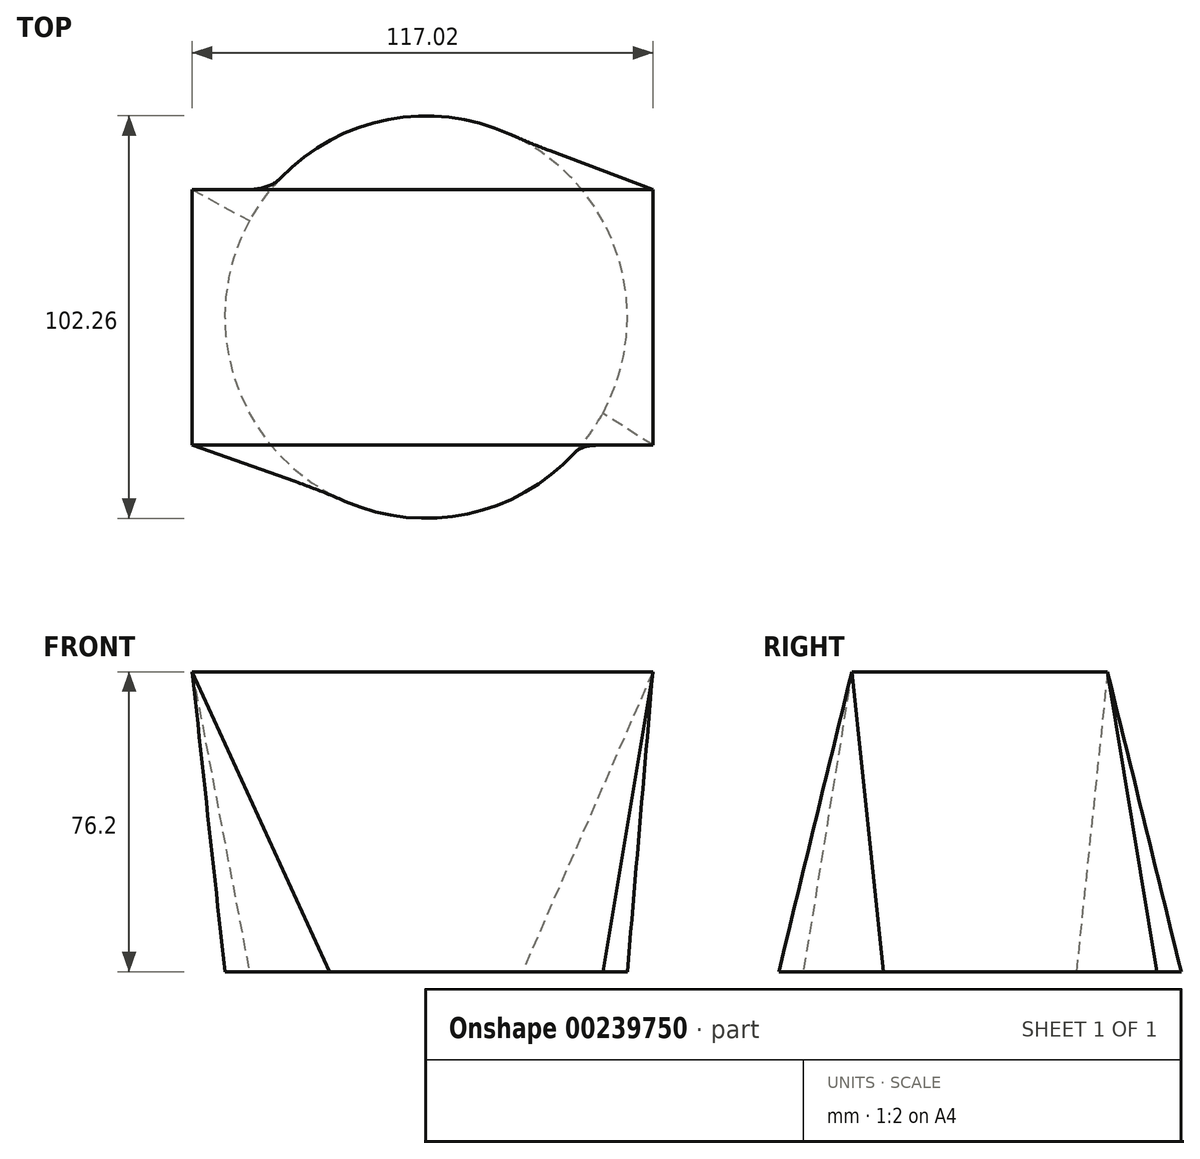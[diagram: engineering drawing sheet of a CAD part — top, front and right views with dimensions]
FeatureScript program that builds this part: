
annotation { "Feature Type Name" : "Feature", "Feature Type Description" : "" }
export const myFeature = defineFeature(function(context is Context, id is Id, definition is map)
    precondition{}
    {
        {
            var Q0;
            Q0=qCreatedBy(makeId("Top.planeOp"),FACE);
            cPlane(context, id + "F0", {"entities" : qUnion([Q0]), "cplaneType" : CPlaneType.OFFSET, "offset" : 76.2 * mm, "width" : 152.4 * mm, "height" : 152.4 * mm});
        }
        {
            var Q0;
            Q0=qCreatedBy(id+"F0.planeOp",FACE);
            var sketch = newSketch(context, id + "F1", { "sketchPlane" : qUnion([Q0])});
            skLineSegment(sketch, "E0.bottom", {"start": v(-59.43, 32.4) * mm, "end": v(57.59, 32.4) * mm});
            skLineSegment(sketch, "E0.top", {"start": v(-59.43, -32.58) * mm, "end": v(57.59, -32.58) * mm});
            skLineSegment(sketch, "E0.left", {"start": v(-59.43, 32.4) * mm, "end": v(-59.43, -32.58) * mm});
            skLineSegment(sketch, "E0.right", {"start": v(57.59, 32.4) * mm, "end": v(57.59, -32.58) * mm});
            skSolve(sketch);
        }
        {
            var Q0;
            Q0=qCreatedBy(makeId("Top.planeOp"),FACE);
            var sketch = newSketch(context, id + "F2", { "sketchPlane" : qUnion([Q0])});
            skCircle(sketch, "E1", {"center": v(0, 0) * mm, "radius": 51.13 * mm});
            skSolve(sketch);
        }
        {
            var Q0;
            Q0=makeQuery(id+"F1.imprint","IMPRINT",FACE,{"disambiguationData":[TD([[makeQuery(id+"F1.imprint","IMPRINT",EDGE,{"derivedFrom":sQuery(id+"F1.wireOp",EDGE,"E0.bottom")}),-1.0]])]});
            var Q1;
            Q1=makeQuery(id+"F2.imprint","IMPRINT",FACE,{"disambiguationData":[TD([[makeQuery(id+"F2.imprint","IMPRINT",EDGE,{"derivedFrom":sQuery(id+"F2.wireOp",EDGE,"E1")}),1.0]])]});
            loft(context, id + "F3", {"sheetProfilesArray" : [{ "sheetProfileEntities" : qUnion([Q0]) }, { "sheetProfileEntities" : qUnion([Q1]) }]});
        }
    });
